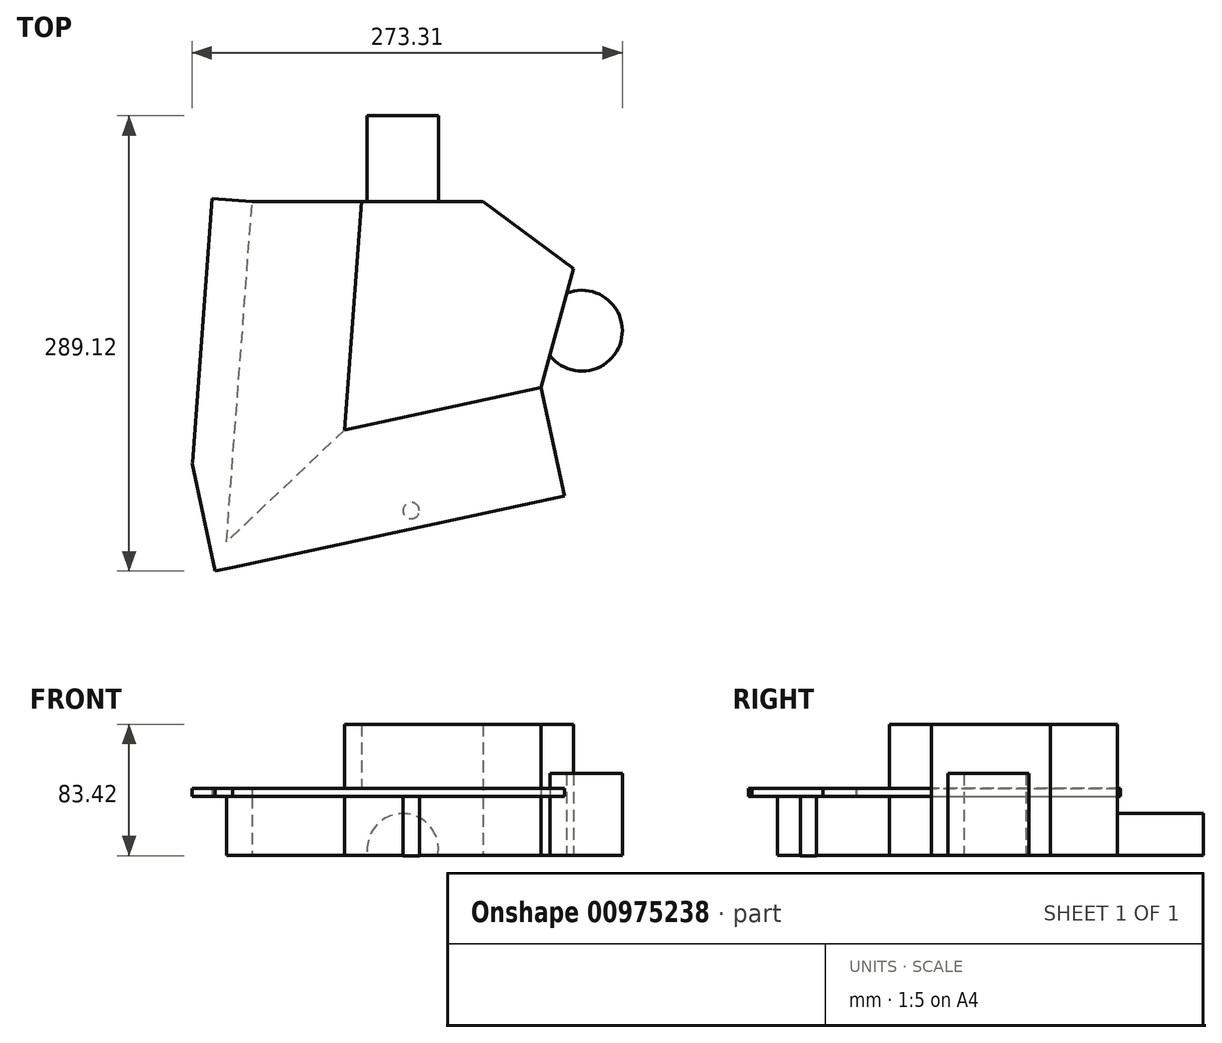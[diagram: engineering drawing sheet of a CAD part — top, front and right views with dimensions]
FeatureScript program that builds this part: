
annotation { "Feature Type Name" : "Feature", "Feature Type Description" : "" }
export const myFeature = defineFeature(function(context is Context, id is Id, definition is map)
    precondition{}
    {
        {
            var Q0;
            Q0=qCreatedBy(makeId("Top.planeOp"),FACE);
            var sketch = newSketch(context, id + "F0", { "sketchPlane" : qUnion([Q0])});
            skLineSegment(sketch, "E0", {"start": v(-59.32, -47.39) * mm, "end": v(65.5, -20.56) * mm});
            skLineSegment(sketch, "E1", {"start": v(65.5, -20.56) * mm, "end": v(86.06, 55.14) * mm});
            skLineSegment(sketch, "E2", {"start": v(86.06, 55.14) * mm, "end": v(28.8, 97.6) * mm});
            skLineSegment(sketch, "E3", {"start": v(28.8, 97.6) * mm, "end": v(-117.95, 97.6) * mm});
            skLineSegment(sketch, "E4", {"start": v(-117.95, 97.6) * mm, "end": v(-134.23, -118.4) * mm});
            skLineSegment(sketch, "E5", {"start": v(-134.23, -118.4) * mm, "end": v(-59.32, -47.39) * mm});
            skSolve(sketch);
        }
        {
            var Q0;
            Q0=makeQuery(id+"F0.imprint","IMPRINT",FACE,{"disambiguationData":[TD([[makeQuery(id+"F0.imprint","IMPRINT",EDGE,{"derivedFrom":sQuery(id+"F0.wireOp",EDGE,"E0")}),1.0]])]});
            extrude(context, id + "F1", {"entities" : qUnion([Q0]), "depth" : 42.42 * mm, "offsetDistance" : 25.4 * mm});
        }
        {
            var Q0;
            Q0=makeQuery(id+"F1.opExtrude","CAP_FACE",FACE,{"disambiguationData":[OSD([sQuery(id+"F0.wireOp",EDGE,"E0"),sQuery(id+"F0.wireOp",EDGE,"E1"),sQuery(id+"F0.wireOp",EDGE,"E2"),sQuery(id+"F0.wireOp",EDGE,"E3"),sQuery(id+"F0.wireOp",EDGE,"E4"),sQuery(id+"F0.wireOp",EDGE,"E5")])],"isStart":false});
            var sketch = newSketch(context, id + "F2", { "sketchPlane" : qUnion([Q0])});
            skLineSegment(sketch, "E6", {"start": v(-59.32, -47.39) * mm, "end": v(-48.4, 97.6) * mm});
            skSolve(sketch);
        }
        {
            var Q0;
            {var subQ1=sQuery(id+"F2.wireOp",EDGE,"E6");Q0=makeQuery(id+"F2.imprint","IMPRINT",FACE,{"disambiguationData":[TD([[makeQuery(id+"F2.imprint","IMPRINT",EDGE,{"derivedFrom":subQ1}),-1.0]])]});}
            extrude(context, id + "F3", {"entities" : qUnion([Q0]), "operationType" : NewBodyOperationType.ADD, "depth" : 40.64 * mm, "offsetDistance" : 25.4 * mm});
        }
        {
            var Q0;
            Q0=makeQuery(id+"F1.opExtrude","SWEPT_FACE",FACE,{"disambiguationData":[OSD([sQuery(id+"F0.wireOp",EDGE,"E5")])]});
            var sketch = newSketch(context, id + "F4", { "sketchPlane" : qUnion([Q0])});
            skLineSegment(sketch, "E7.bottom", {"start": v(-137.57, 22.97) * mm, "end": v(-121.72, 22.97) * mm});
            skLineSegment(sketch, "E7.top", {"start": v(-137.57, 0) * mm, "end": v(-121.72, 0) * mm});
            skLineSegment(sketch, "E7.left", {"start": v(-137.57, 22.97) * mm, "end": v(-137.57, 0) * mm});
            skLineSegment(sketch, "E7.right", {"start": v(-121.72, 22.97) * mm, "end": v(-121.72, 0) * mm});
            skSolve(sketch);
        }
        {
            var Q0;
            Q0=makeQuery(id+"F1.opExtrude","CAP_FACE",FACE,{"disambiguationData":[OSD([sQuery(id+"F0.wireOp",EDGE,"E0"),sQuery(id+"F0.wireOp",EDGE,"E1"),sQuery(id+"F0.wireOp",EDGE,"E2"),sQuery(id+"F0.wireOp",EDGE,"E3"),sQuery(id+"F0.wireOp",EDGE,"E4"),sQuery(id+"F0.wireOp",EDGE,"E5")])],"isStart":true});
            var sketch = newSketch(context, id + "F5", { "sketchPlane" : qUnion([Q0])});
            skArc(sketch, "E8", {"start": v(81.8, -39.45) * mm, "mid": v(116.24, -8.9) * mm, "end": v(71.08, 0) * mm});
            skSolve(sketch);
        }
        {
            var Q0;
            {var subQ0=sQuery(id+"F5.wireOp",EDGE,"E8");Q0=makeQuery(id+"F5.imprint","IMPRINT",FACE,{"disambiguationData":[TD([[makeQuery(id+"F5.imprint","IMPRINT",EDGE,{"derivedFrom":subQ0}),1.0]])]});}
            extrude(context, id + "F6", {"entities" : qUnion([Q0]), "operationType" : NewBodyOperationType.ADD, "oppositeDirection" : true, "depth" : 51.82 * mm, "offsetDistance" : 25.4 * mm});
        }
        {
            var Q0;
            {var subQ0=sQuery(id+"F0.wireOp",EDGE,"E3");Q0=makeQuery(id+"F3.boolean.opBoolean","MERGE",FACE,{"derivedFrom":[makeQuery(id+"F1.opExtrude","SWEPT_FACE",FACE,{"disambiguationData":[OSD([subQ0])]}),makeQuery(id+"F3.opExtrude","SWEPT_FACE",FACE,{"disambiguationData":[OSD([subQ0])]})]});}
            var sketch = newSketch(context, id + "F7", { "sketchPlane" : qUnion([Q0])});
            skArc(sketch, "E9", {"start": v(44.58, 0) * mm, "mid": v(22.29, 26.4) * mm, "end": v(0, 0) * mm});
            skSolve(sketch);
        }
        {
            var Q0;
            {var subQ0=sQuery(id+"F7.wireOp",EDGE,"E9");Q0=makeQuery(id+"F7.imprint","IMPRINT",FACE,{"disambiguationData":[TD([[makeQuery(id+"F7.imprint","IMPRINT",EDGE,{"derivedFrom":subQ0}),1.0]])]});}
            extrude(context, id + "F8", {"entities" : qUnion([Q0]), "operationType" : NewBodyOperationType.ADD, "depth" : 54.6 * mm, "offsetDistance" : 25.4 * mm});
        }
        {
            var Q0;
            {var subQ0=sQuery(id+"F0.wireOp",EDGE,"E0");Q0=makeQuery(id+"F3.boolean.opBoolean","MERGE",FACE,{"derivedFrom":[makeQuery(id+"F1.opExtrude","SWEPT_FACE",FACE,{"disambiguationData":[OSD([subQ0])]}),makeQuery(id+"F3.opExtrude","SWEPT_FACE",FACE,{"disambiguationData":[OSD([subQ0])]})]});}
            var sketch = newSketch(context, id + "F9", { "sketchPlane" : qUnion([Q0])});
            skLineSegment(sketch, "E10", {"start": v(-67.96, 42.42) * mm, "end": v(59.71, 42.42) * mm});
            skLineSegment(sketch, "E11", {"start": v(59.71, 42.42) * mm, "end": v(59.71, 37.23) * mm});
            skLineSegment(sketch, "E12", {"start": v(59.71, 37.23) * mm, "end": v(-67.96, 37.23) * mm});
            skSolve(sketch);
        }
        {
            var Q0;
            {var subQ0=sQuery(id+"F9.wireOp",EDGE,"E10");Q0=makeQuery(id+"F9.imprint","IMPRINT",FACE,{"disambiguationData":[TD([[makeQuery(id+"F9.imprint","IMPRINT",EDGE,{"derivedFrom":subQ0}),-1.0]])]});}
            extrude(context, id + "F10", {"entities" : qUnion([Q0]), "operationType" : NewBodyOperationType.ADD, "depth" : 44.96 * mm, "offsetDistance" : 25.4 * mm});
        }
        {
            var Q0;
            Q0=makeQuery(id+"F10.opExtrude","CAP_FACE",FACE,{"disambiguationData":[OSD([sQuery(id+"F0.wireOp",EDGE,"E0"),sQuery(id+"F0.wireOp",EDGE,"E5"),sQuery(id+"F9.wireOp",EDGE,"E10"),sQuery(id+"F9.wireOp",EDGE,"E11"),sQuery(id+"F9.wireOp",EDGE,"E12")])],"isStart":false});
            extrude(context, id + "F11", {"entities" : qUnion([Q0]), "operationType" : NewBodyOperationType.ADD, "depth" : 25.4 * mm, "offsetDistance" : 25.4 * mm});
        }
        {
            var Q0;
            {var subQ0=sQuery(id+"F0.wireOp",EDGE,"E5");var subQ1=sQuery(id+"F0.wireOp",EDGE,"E0");Q0=makeQuery(id+"F11.boolean.opBoolean","MERGE",FACE,{"derivedFrom":[makeQuery(id+"F10.opExtrude","SWEPT_FACE",FACE,{"disambiguationData":[OSD([subQ1,subQ0])]}),makeQuery(id+"F11.opExtrude","SWEPT_FACE",FACE,{"disambiguationData":[OSD([subQ1,subQ0])]})]});}
            extrude(context, id + "F12", {"entities" : qUnion([Q0]), "operationType" : NewBodyOperationType.ADD, "depth" : 87.88 * mm, "offsetDistance" : 25.4 * mm});
        }
        {
            var Q0;
            Q0=makeQuery(id+"F1.opExtrude","SWEPT_FACE",FACE,{"disambiguationData":[OSD([sQuery(id+"F0.wireOp",EDGE,"E4")])]});
            var sketch = newSketch(context, id + "F13", { "sketchPlane" : qUnion([Q0])});
            skLineSegment(sketch, "E13", {"start": v(72.18, 37.23) * mm, "end": v(-88.45, 37.23) * mm});
            skSolve(sketch);
        }
        {
            var Q0;
            {var subQ0=sQuery(id+"F13.wireOp",EDGE,"E13");Q0=makeQuery(id+"F13.imprint","IMPRINT",FACE,{"disambiguationData":[TD([[makeQuery(id+"F13.imprint","IMPRINT",EDGE,{"derivedFrom":subQ0}),-1.0]])]});}
            extrude(context, id + "F14", {"entities" : qUnion([Q0]), "operationType" : NewBodyOperationType.ADD, "depth" : 25.4 * mm, "offsetDistance" : 25.4 * mm});
        }
        {
            var Q0;
            {var subQ1=sQuery(id+"F0.wireOp",EDGE,"E5");var subQ2=sQuery(id+"F0.wireOp",EDGE,"E0");var subQ3=sQuery(id+"F0.wireOp",EDGE,"E4");Q0=makeQuery(id+"F12.boolean.opBoolean","SPLIT",FACE,{"disambiguationData":[TD([makeQuery(id+"F1.opExtrude","SWEPT_FACE",FACE,{"disambiguationData":[OSD([subQ3])]})])],"derivedFrom":makeQuery(id+"F12.opExtrude","CAP_FACE",FACE,{"disambiguationData":[OSD([subQ2,subQ1])],"isStart":false})});}
            extrude(context, id + "F15", {"entities" : qUnion([Q0]), "operationType" : NewBodyOperationType.ADD, "depth" : 11.18 * mm, "offsetDistance" : 25.4 * mm});
        }
        {
            var Q0;
            Q0=makeQuery(id+"F15.opExtrude","SWEPT_FACE",FACE,{"disambiguationData":[OSD([sQuery(id+"F0.wireOp",EDGE,"E0"),sQuery(id+"F0.wireOp",EDGE,"E4"),sQuery(id+"F0.wireOp",EDGE,"E5")])]});
            extrude(context, id + "F16", {"entities" : qUnion([Q0]), "operationType" : NewBodyOperationType.ADD, "depth" : 17.53 * mm, "offsetDistance" : 25.4 * mm});
        }
        {
            var Q0;
            Q0=makeQuery(id+"F14.opExtrude","SWEPT_FACE",FACE,{"disambiguationData":[OSD([sQuery(id+"F0.wireOp",EDGE,"E0"),sQuery(id+"F0.wireOp",EDGE,"E4"),sQuery(id+"F0.wireOp",EDGE,"E5")])]});
            extrude(context, id + "F17", {"entities" : qUnion([Q0]), "operationType" : NewBodyOperationType.ADD, "depth" : 8.13 * mm, "offsetDistance" : 25.4 * mm});
        }
        {
            var Q0;
            {var subQ0=sQuery(id+"F13.wireOp",EDGE,"E13");var subQ1=sQuery(id+"F9.wireOp",EDGE,"E12");var subQ2=sQuery(id+"F0.wireOp",EDGE,"E5");var subQ3=sQuery(id+"F0.wireOp",EDGE,"E4");var subQ4=sQuery(id+"F0.wireOp",EDGE,"E0");var subQ5=makeQuery(id+"F12.opExtrude","SWEPT_FACE",FACE,{"disambiguationData":[OSD([subQ4,subQ2,subQ1])]});Q0=makeQuery(id+"F17.boolean.opBoolean","MERGE",FACE,{"derivedFrom":[makeQuery(id+"F14.opExtrude","SWEPT_FACE",FACE,{"disambiguationData":[OSD([subQ0])]}),makeQuery(id+"F16.boolean.opBoolean","MERGE",FACE,{"derivedFrom":[makeQuery(id+"F12.boolean.opBoolean","MERGE",FACE,{"derivedFrom":[makeQuery(id+"F11.boolean.opBoolean","MERGE",FACE,{"derivedFrom":[makeQuery(id+"F10.opExtrude","SWEPT_FACE",FACE,{"disambiguationData":[OSD([subQ1])]}),makeQuery(id+"F11.opExtrude","SWEPT_FACE",FACE,{"disambiguationData":[OSD([subQ1])]})]}),subQ5]}),makeQuery(id+"F15.boolean.opBoolean","MERGE",FACE,{"derivedFrom":[makeQuery(id+"F12.boolean.opBoolean","SPLIT",FACE,{"derivedFrom":subQ5}),makeQuery(id+"F15.opExtrude","SWEPT_FACE",FACE,{"disambiguationData":[OSD([subQ4,subQ2,subQ1])]})]}),makeQuery(id+"F16.opExtrude","SWEPT_FACE",FACE,{"disambiguationData":[OSD([subQ4,subQ3,subQ2,subQ1])]})]}),makeQuery(id+"F17.opExtrude","SWEPT_FACE",FACE,{"disambiguationData":[OSD([subQ4,subQ3,subQ2,subQ1,subQ0])]})]});}
            var sketch = newSketch(context, id + "F18", { "sketchPlane" : qUnion([Q0])});
            skCircle(sketch, "E14", {"center": v(-16.93, 98.61) * mm, "radius": 5.15 * mm});
            skSolve(sketch);
        }
        {
            var Q0;
            Q0=makeQuery(id+"F18.imprint","IMPRINT",FACE,{"disambiguationData":[TD([[makeQuery(id+"F18.imprint","IMPRINT",EDGE,{"derivedFrom":sQuery(id+"F18.wireOp",EDGE,"E14")}),1.0]])]});
            extrude(context, id + "F19", {"entities" : qUnion([Q0]), "operationType" : NewBodyOperationType.ADD, "depth" : 37.6 * mm, "offsetDistance" : 25.4 * mm});
        }
    });
